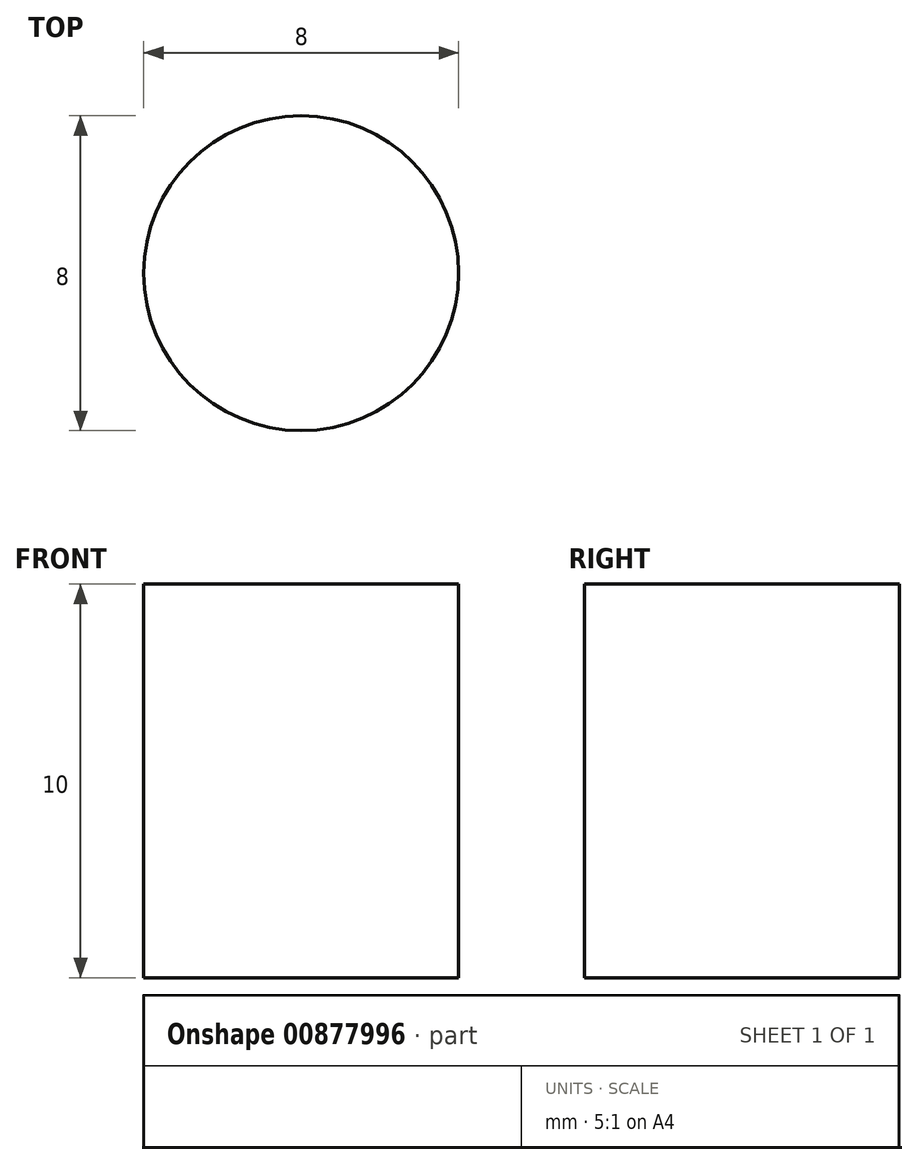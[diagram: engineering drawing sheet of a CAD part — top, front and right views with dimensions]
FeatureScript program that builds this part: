
annotation { "Feature Type Name" : "Feature", "Feature Type Description" : "" }
export const myFeature = defineFeature(function(context is Context, id is Id, definition is map)
    precondition{}
    {
        {
            var Q0;
            Q0=qCreatedBy(makeId("Top.planeOp"),FACE);
            var sketch = newSketch(context, id + "F0", { "sketchPlane" : qUnion([Q0])});
            skCircle(sketch, "E0", {"center": v(0, 0) * mm, "radius": 4 * mm});
            skSolve(sketch);
        }
        {
            var Q0;
            Q0 = qSketchRegion(id + "F0", true);
            extrude(context, id + "F1", {"entities" : qUnion([Q0]), "depth" : 10 * mm, "offsetDistance" : 25 * mm});
        }
    });
